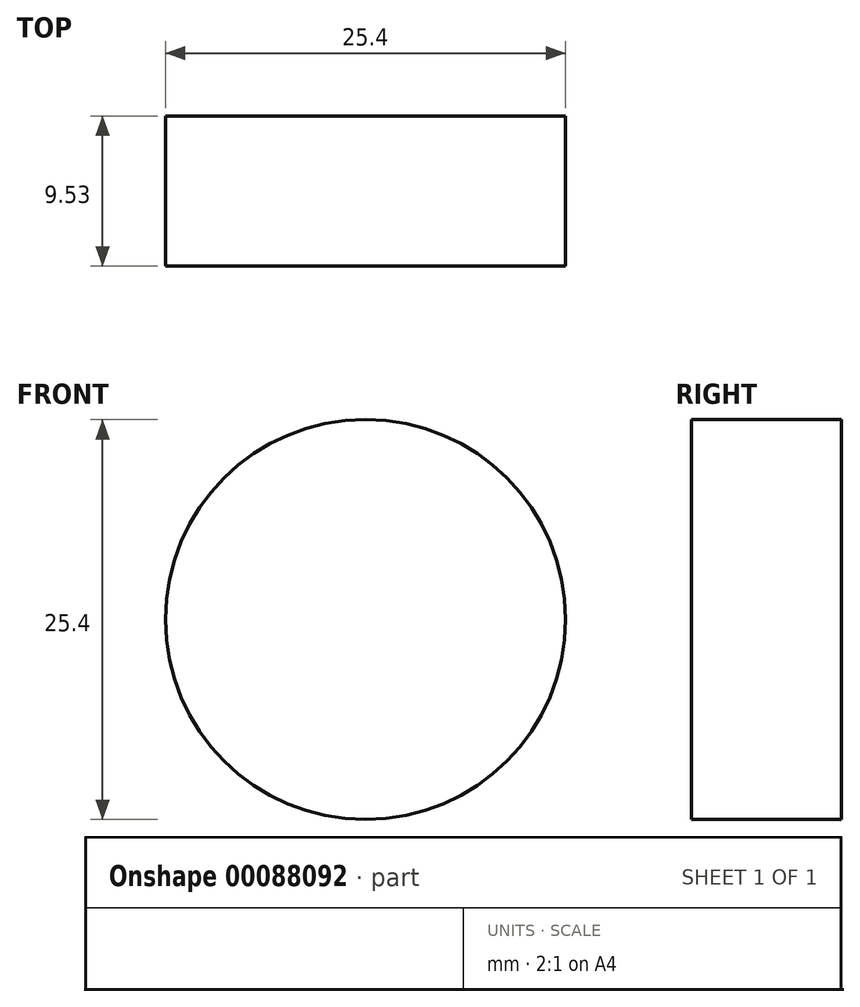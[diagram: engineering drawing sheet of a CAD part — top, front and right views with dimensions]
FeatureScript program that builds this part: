
annotation { "Feature Type Name" : "Feature", "Feature Type Description" : "" }
export const myFeature = defineFeature(function(context is Context, id is Id, definition is map)
    precondition{}
    {
        {
            var Q0;
            Q0=qCreatedBy(makeId("Right.planeOp"),FACE);
            var sketch = newSketch(context, id + "F0", { "sketchPlane" : qUnion([Q0])});
            skLineSegment(sketch, "E0.bottom", {"start": v(-9.53, 69.85) * mm, "end": v(9.52, 69.85) * mm});
            skLineSegment(sketch, "E0.top", {"start": v(-9.52, -69.85) * mm, "end": v(9.53, -69.85) * mm});
            skLineSegment(sketch, "E0.left", {"start": v(-9.53, 69.85) * mm, "end": v(-9.52, -69.85) * mm});
            skLineSegment(sketch, "E0.right", {"start": v(9.52, 69.85) * mm, "end": v(9.53, -69.85) * mm});
            skSolve(sketch);
        }
        {
            var Q0;
            Q0=makeQuery(id+"F0.imprint","IMPRINT",FACE,{"disambiguationData":[TD([[makeQuery(id+"F0.imprint","IMPRINT",EDGE,{"derivedFrom":sQuery(id+"F0.wireOp",EDGE,"E0.bottom")}),-1.0]])]});
            extrude(context, id + "F1", {"entities" : qUnion([Q0]), "endBound" : BoundingType.SYMMETRIC, "depth" : 889 * mm});
        }
        {
            var Q0;
            Q0=makeQuery(id+"F1.opExtrude","SWEPT_FACE",FACE,{"disambiguationData":[OSD([sQuery(id+"F0.wireOp",EDGE,"E0.left")])]});
            var sketch = newSketch(context, id + "F2", { "sketchPlane" : qUnion([Q0])});
            skLineSegment(sketch, "E1", {"start": v(328.3, -6.35) * mm, "end": v(444.5, -6.35) * mm, "construction": true});
            skLineSegment(sketch, "E2", {"start": v(393.7, 69.85) * mm, "end": v(393.7, -69.85) * mm, "construction": true});
            skLineSegment(sketch, "E3", {"start": v(327.92, 0) * mm, "end": v(444.5, 0) * mm, "construction": true});
            skLineSegment(sketch, "E4", {"start": v(327.92, -12.7) * mm, "end": v(444.5, -12.7) * mm, "construction": true});
            skCircle(sketch, "E5", {"center": v(393.7, -12.7) * mm, "radius": 12.7 * mm});
            skLineSegment(sketch, "E6", {"start": v(0, 69.85) * mm, "end": v(0, -69.85) * mm, "construction": true});
            skCircle(sketch, "E7.MirrorC", {"center": v(-393.7, -12.7) * mm, "radius": 12.7 * mm});
            skSolve(sketch);
        }
        {
            var Q0;
            Q0=makeQuery(id+"F2.imprint","IMPRINT",FACE,{"disambiguationData":[TD([[makeQuery(id+"F2.imprint","IMPRINT",EDGE,{"derivedFrom":sQuery(id+"F2.wireOp",EDGE,"E7.MirrorC")}),-1.0]])]});
            var Q1;
            Q1=makeQuery(id+"F2.imprint","IMPRINT",FACE,{"disambiguationData":[TD([[makeQuery(id+"F2.imprint","IMPRINT",EDGE,{"derivedFrom":sQuery(id+"F2.wireOp",EDGE,"E5")}),1.0]])]});
            extrude(context, id + "F3", {"entities" : qUnion([Q0, Q1]), "operationType" : NewBodyOperationType.REMOVE, "endBound" : BoundingType.THROUGH_ALL, "oppositeDirection" : true, "depth" : 25.4 * mm});
        }
        {
            var Q0;
            Q0=makeQuery(id+"F1.opExtrude","SWEPT_FACE",FACE,{"disambiguationData":[OSD([sQuery(id+"F0.wireOp",EDGE,"E0.left")])]});
            var sketch = newSketch(context, id + "F4", { "sketchPlane" : qUnion([Q0])});
            skCircle(sketch, "E8.0", {"center": v(-393.7, -12.7) * mm, "radius": 12.7 * mm});
            skCircle(sketch, "E9.0", {"center": v(393.7, -12.7) * mm, "radius": 12.7 * mm});
            skCircle(sketch, "E10", {"center": v(-393.7, -12.7) * mm, "radius": 17.15 * mm});
            skCircle(sketch, "E11", {"center": v(393.7, -12.7) * mm, "radius": 17.15 * mm});
            skSolve(sketch);
        }
        {
            var Q0;
            Q0=makeQuery(id+"F4.imprint","IMPRINT",FACE,{"disambiguationData":[TD([[makeQuery(id+"F4.imprint","IMPRINT",EDGE,{"derivedFrom":sQuery(id+"F4.wireOp",EDGE,"E8.0")}),1.0]])]});
            var Q1;
            Q1=makeQuery(id+"F4.imprint","IMPRINT",FACE,{"disambiguationData":[TD([[makeQuery(id+"F4.imprint","IMPRINT",EDGE,{"derivedFrom":sQuery(id+"F4.wireOp",EDGE,"E9.0")}),-1.0]])]});
            extrude(context, id + "F5", {"entities" : qUnion([Q0, Q1]), "operationType" : NewBodyOperationType.REMOVE, "oppositeDirection" : true, "depth" : 9.52 * mm});
        }
    });
